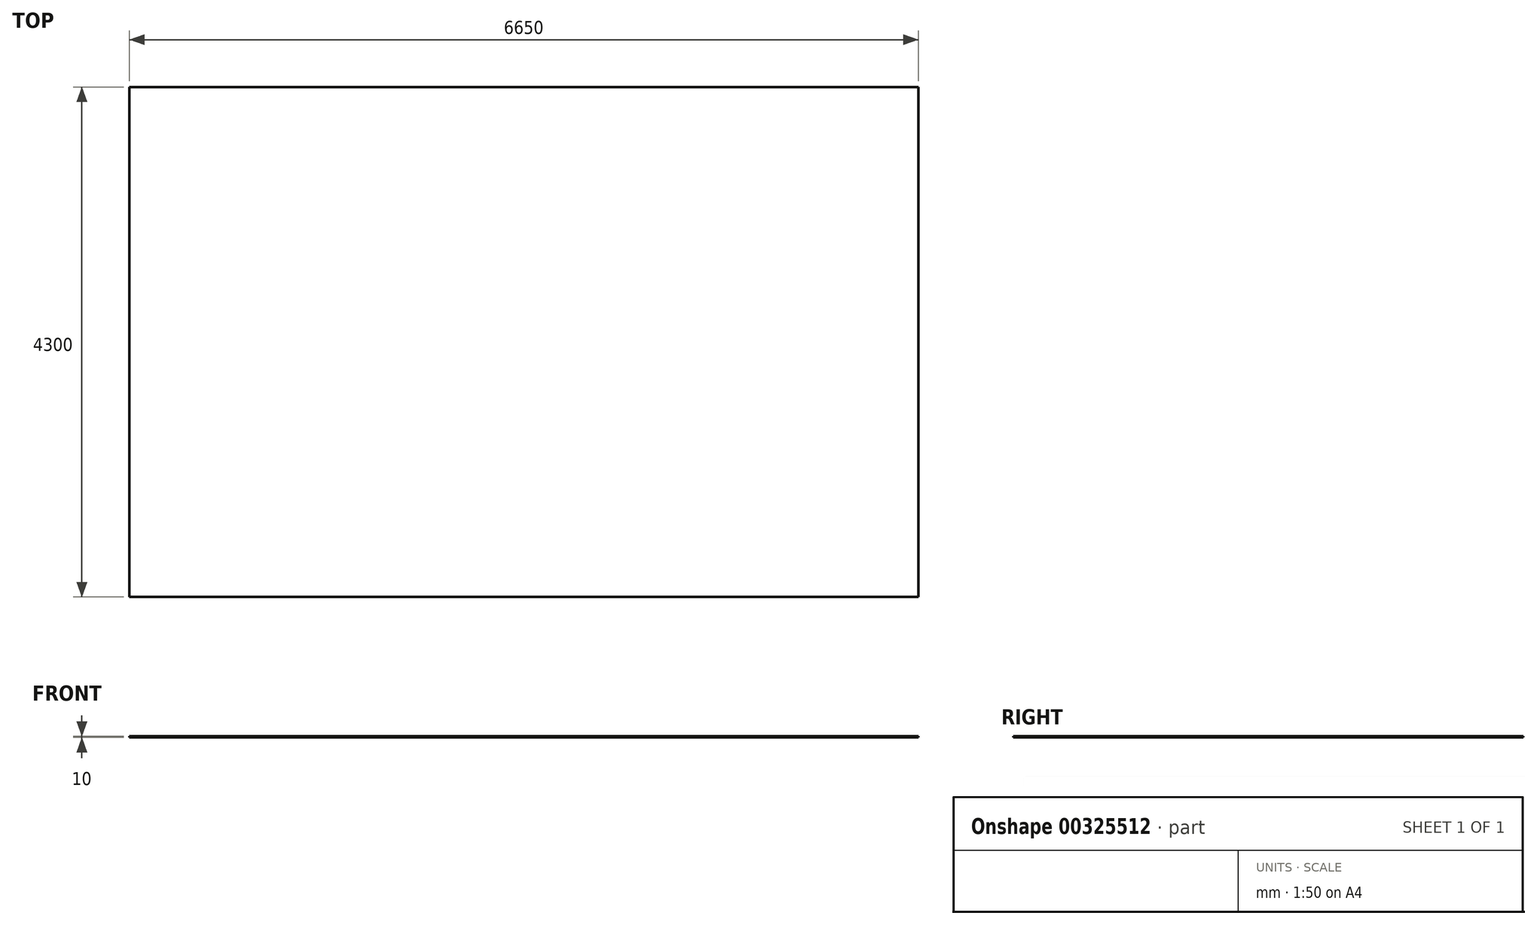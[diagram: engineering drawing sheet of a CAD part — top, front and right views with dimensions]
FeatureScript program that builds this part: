
annotation { "Feature Type Name" : "Feature", "Feature Type Description" : "" }
export const myFeature = defineFeature(function(context is Context, id is Id, definition is map)
    precondition{}
    {
        {
            var Q0;
            Q0=qCreatedBy(makeId("Top.planeOp"),FACE);
            var sketch = newSketch(context, id + "F0", { "sketchPlane" : qUnion([Q0])});
            skLineSegment(sketch, "E0.bottom", {"start": v(3424.42, -2150) * mm, "end": v(-3225.58, -2150) * mm});
            skLineSegment(sketch, "E0.top", {"start": v(3424.42, 2150) * mm, "end": v(-3225.58, 2150) * mm});
            skLineSegment(sketch, "E0.left", {"start": v(3424.42, -2150) * mm, "end": v(3424.42, 2150) * mm});
            skLineSegment(sketch, "E0.right", {"start": v(-3225.58, -2150) * mm, "end": v(-3225.58, 2150) * mm});
            skPoint(sketch, "E0.middle", {"position": v(99.42, 0) * mm});
            skSolve(sketch);
        }
        {
            var Q0;
            Q0 = qSketchRegion(id + "F0", true);
            extrude(context, id + "F1", {"entities" : qUnion([Q0]), "depth" : 10 * mm});
        }
    });
